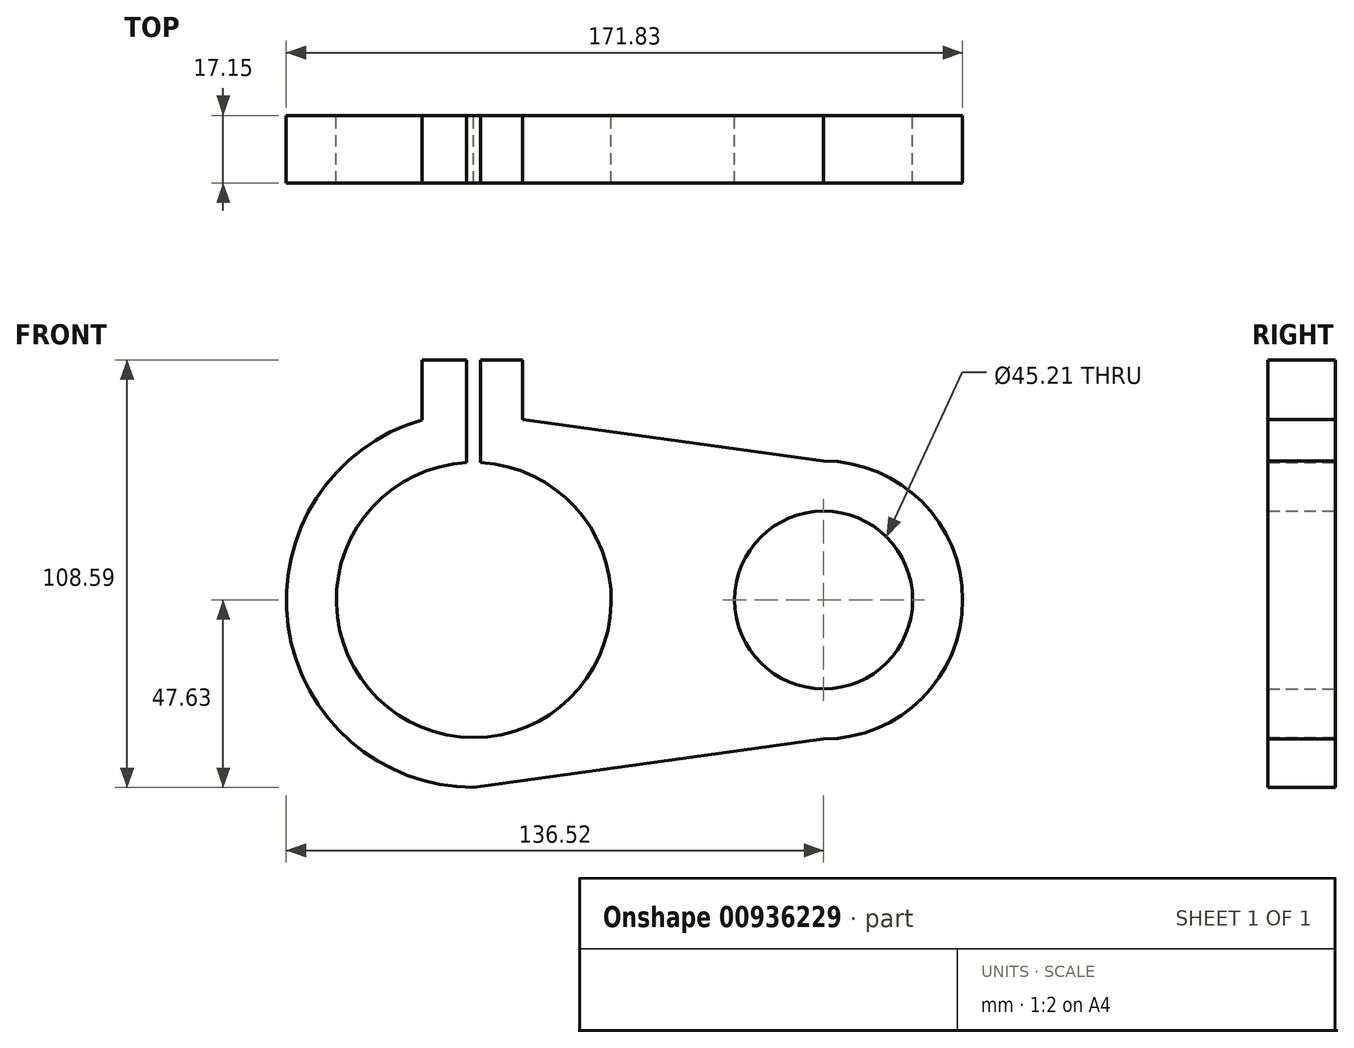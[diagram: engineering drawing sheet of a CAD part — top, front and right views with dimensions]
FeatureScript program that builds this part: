
annotation { "Feature Type Name" : "Feature", "Feature Type Description" : "" }
export const myFeature = defineFeature(function(context is Context, id is Id, definition is map)
    precondition{}
    {
        {
            var Q0;
            Q0=qCreatedBy(makeId("Front.planeOp"),FACE);
            var sketch = newSketch(context, id + "F0", { "sketchPlane" : qUnion([Q0])});
            skCircle(sketch, "E0", {"center": v(0, 0) * mm, "radius": 34.93 * mm});
            skArc(sketch, "E1", {"start": v(0, 47.63) * mm, "mid": v(-47.63, 0) * mm, "end": v(0, -47.63) * mm});
            skCircle(sketch, "E2", {"center": v(88.9, 0) * mm, "radius": 22.6 * mm});
            skLineSegment(sketch, "E3", {"start": v(88.9, -36.13) * mm, "end": v(88.9, 48.6) * mm, "construction": true});
            skArc(sketch, "E4", {"start": v(88.9, 35.3) * mm, "mid": v(124.2, 0) * mm, "end": v(88.9, -35.3) * mm});
            skLineSegment(sketch, "E5", {"start": v(0, 47.62) * mm, "end": v(88.9, 35.3) * mm});
            skLineSegment(sketch, "E6", {"start": v(0, -47.63) * mm, "end": v(88.9, -35.3) * mm});
            skLineSegment(sketch, "E7", {"start": v(-1.78, 34.88) * mm, "end": v(-1.78, 47.6) * mm});
            skLineSegment(sketch, "E8", {"start": v(-1.78, 47.6) * mm, "end": v(-1.78, 60.96) * mm});
            skLineSegment(sketch, "E9", {"start": v(-1.78, 60.96) * mm, "end": v(-13.1, 60.96) * mm});
            skLineSegment(sketch, "E10", {"start": v(-13.1, 60.96) * mm, "end": v(-13.1, 45.79) * mm});
            skLineSegment(sketch, "E11", {"start": v(1.78, 34.88) * mm, "end": v(1.78, 60.96) * mm});
            skLineSegment(sketch, "E12", {"start": v(1.78, 60.96) * mm, "end": v(12.34, 60.96) * mm});
            skLineSegment(sketch, "E13", {"start": v(12.34, 60.96) * mm, "end": v(12.34, 45.92) * mm});
            skLineSegment(sketch, "E14", {"start": v(-37.52, 60.96) * mm, "end": v(37.78, 60.96) * mm, "construction": true});
            skSolve(sketch);
        }
        {
            var Q0;
            Q0=makeQuery(id+"F0.imprint","IMPRINT",FACE,{"disambiguationData":[TD([[makeQuery(id+"F0.imprint","IMPRINT",EDGE,{"derivedFrom":sQuery(id+"F0.wireOp",EDGE,"E2")}),-1.0]])]});
            var Q1;
            Q1=makeQuery(id+"F0.imprint","IMPRINT",FACE,{"disambiguationData":[TD([[makeQuery(id+"F0.imprint","IMPRINT",EDGE,{"derivedFrom":sQuery(id+"F0.wireOp",EDGE,"Wh4SmWdp-UOKD-iHl2-3teP-QEHY2wbws6r0")}),1.0]])]});
            var Q2;
            {var subQ0=sQuery(id+"F0.wireOp",EDGE,"E8");Q2=makeQuery(id+"F0.imprint","IMPRINT",FACE,{"disambiguationData":[TD([[makeQuery(id+"F0.imprint","IMPRINT",EDGE,{"derivedFrom":subQ0}),1.0]])]});}
            var Q3;
            {var subQ4=sQuery(id+"F0.wireOp",EDGE,"E12");Q3=makeQuery(id+"F0.imprint","IMPRINT",FACE,{"disambiguationData":[TD([[makeQuery(id+"F0.imprint","IMPRINT",EDGE,{"derivedFrom":subQ4}),-1.0]])]});}
            var Q4;
            {var subQ9=sQuery(id+"F0.wireOp",EDGE,"E4");Q4=makeQuery(id+"F0.imprint","IMPRINT",FACE,{"disambiguationData":[TD([[makeQuery(id+"F0.imprint","IMPRINT",EDGE,{"derivedFrom":subQ9}),-1.0]])]});}
            extrude(context, id + "F1", {"entities" : qUnion([Q0, Q1, Q2, Q3, Q4]), "depth" : 17.14 * mm, "offsetDistance" : 25.4 * mm});
        }
    });
